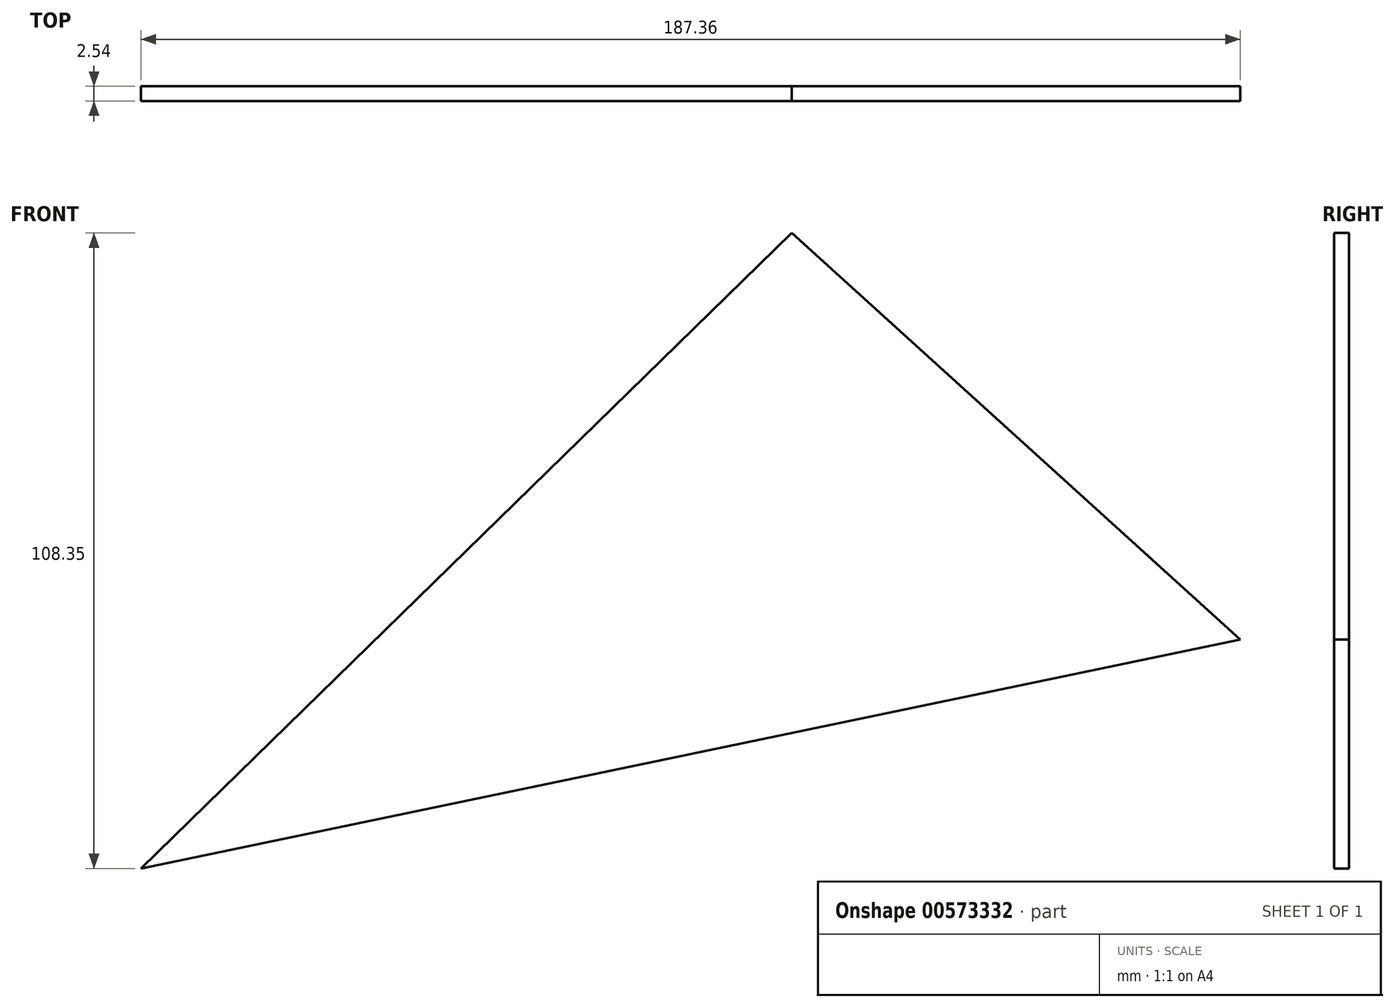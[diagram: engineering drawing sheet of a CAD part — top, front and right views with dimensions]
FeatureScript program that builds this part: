
annotation { "Feature Type Name" : "Feature", "Feature Type Description" : "" }
export const myFeature = defineFeature(function(context is Context, id is Id, definition is map)
    precondition{}
    {
        {
            var Q0;
            Q0=qCreatedBy(makeId("Front.planeOp"),FACE);
            var sketch = newSketch(context, id + "F0", { "sketchPlane" : qUnion([Q0])});
            skLineSegment(sketch, "E0", {"start": v(-98.9, 10) * mm, "end": v(88.45, 49.06) * mm});
            skLineSegment(sketch, "E1", {"start": v(12.03, 118.36) * mm, "end": v(88.45, 49.06) * mm});
            skLineSegment(sketch, "E2", {"start": v(12.03, 118.36) * mm, "end": v(-98.9, 10) * mm});
            skSolve(sketch);
        }
        {
            var Q0;
            Q0=makeQuery(id+"F0.imprint","IMPRINT",FACE,{"disambiguationData":[TD([[makeQuery(id+"F0.imprint","IMPRINT",EDGE,{"derivedFrom":sQuery(id+"F0.wireOp",EDGE,"E0")}),1.0]])]});
            extrude(context, id + "F1", {"entities" : qUnion([Q0]), "depth" : 2.54 * mm, "offsetDistance" : 25.4 * mm});
        }
    });
